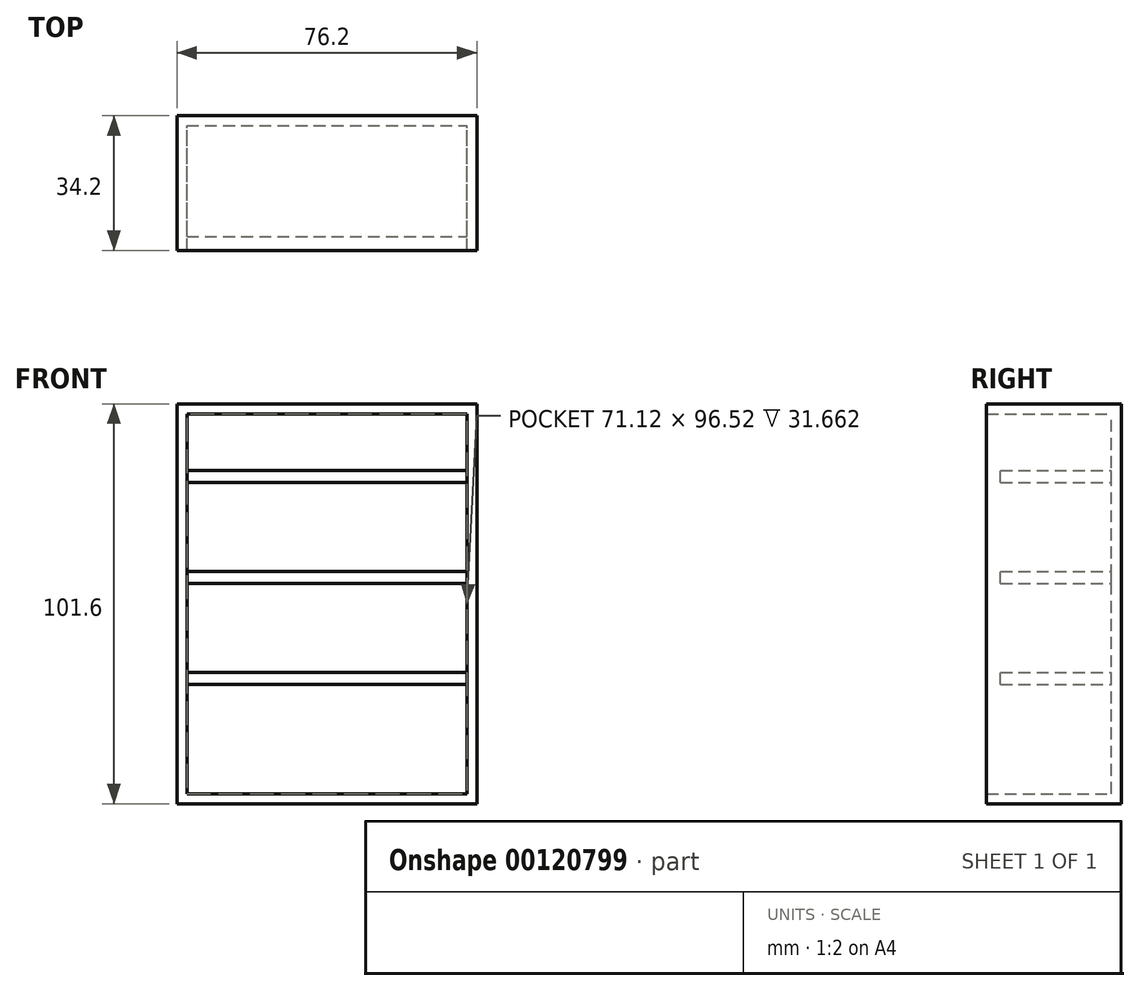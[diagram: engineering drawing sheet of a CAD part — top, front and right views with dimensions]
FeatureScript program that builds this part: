
annotation { "Feature Type Name" : "Feature", "Feature Type Description" : "" }
export const myFeature = defineFeature(function(context is Context, id is Id, definition is map)
    precondition{}
    {
        {
            var Q0;
            Q0=qCreatedBy(makeId("Front.planeOp"),FACE);
            var sketch = newSketch(context, id + "F0", { "sketchPlane" : qUnion([Q0])});
            skLineSegment(sketch, "E0.bottom", {"start": v(0, 0) * mm, "end": v(-76.2, 0) * mm});
            skLineSegment(sketch, "E0.top", {"start": v(0, 101.6) * mm, "end": v(-76.2, 101.6) * mm});
            skLineSegment(sketch, "E0.left", {"start": v(0, 0) * mm, "end": v(0, 101.6) * mm});
            skLineSegment(sketch, "E0.right", {"start": v(-76.2, 0) * mm, "end": v(-76.2, 101.6) * mm});
            skSolve(sketch);
        }
        {
            var Q0;
            Q0=makeQuery(id+"F0.imprint","IMPRINT",FACE,{"disambiguationData":[TD([[makeQuery(id+"F0.imprint","IMPRINT",EDGE,{"derivedFrom":sQuery(id+"F0.wireOp",EDGE,"E0.bottom")}),-1.0]])]});
            extrude(context, id + "F1", {"entities" : qUnion([Q0]), "depth" : 34.2 * mm});
        }
        {
            var Q0;
            Q0=makeQuery(id+"F1.opExtrude","CAP_FACE",FACE,{"disambiguationData":[OSD([sQuery(id+"F0.wireOp",EDGE,"E0.bottom"),sQuery(id+"F0.wireOp",EDGE,"E0.top"),sQuery(id+"F0.wireOp",EDGE,"E0.left"),sQuery(id+"F0.wireOp",EDGE,"E0.right")])],"isStart":false});
            shell(context, id + "F2", {"entities" : qUnion([Q0]), "thickness" : 2.54 * mm});
        }
        {
            var Q0;
            Q0=makeQuery(id+"F2.opShell","OFFSET_FACE",FACE,{"disambiguationData":[OSD([sQuery(id+"F0.wireOp",EDGE,"E0.bottom"),sQuery(id+"F0.wireOp",EDGE,"E0.top"),sQuery(id+"F0.wireOp",EDGE,"E0.left"),sQuery(id+"F0.wireOp",EDGE,"E0.right")])]});
            var sketch = newSketch(context, id + "F3", { "sketchPlane" : qUnion([Q0])});
            skLineSegment(sketch, "E1", {"start": v(-73.66, 84.65) * mm, "end": v(-2.54, 84.65) * mm});
            skLineSegment(sketch, "E2", {"start": v(-2.54, 84.65) * mm, "end": v(-2.54, 81.6) * mm});
            skLineSegment(sketch, "E3", {"start": v(-2.54, 81.6) * mm, "end": v(-73.66, 81.6) * mm});
            skLineSegment(sketch, "E4", {"start": v(-73.66, 81.6) * mm, "end": v(-73.66, 84.65) * mm});
            skLineSegment(sketch, "E5", {"start": v(-73.66, 59) * mm, "end": v(-2.54, 59) * mm});
            skLineSegment(sketch, "E6", {"start": v(-2.54, 59) * mm, "end": v(-2.54, 55.95) * mm});
            skLineSegment(sketch, "E7", {"start": v(-2.54, 55.95) * mm, "end": v(-73.66, 55.95) * mm});
            skLineSegment(sketch, "E8", {"start": v(-73.66, 55.95) * mm, "end": v(-73.66, 59) * mm});
            skLineSegment(sketch, "E9", {"start": v(-73.66, 33.35) * mm, "end": v(-2.54, 33.35) * mm});
            skLineSegment(sketch, "E10", {"start": v(-2.54, 33.35) * mm, "end": v(-2.54, 30.3) * mm});
            skLineSegment(sketch, "E11", {"start": v(-2.54, 30.3) * mm, "end": v(-73.66, 30.3) * mm});
            skLineSegment(sketch, "E12", {"start": v(-73.66, 30.3) * mm, "end": v(-73.66, 33.35) * mm});
            skSolve(sketch);
        }
        {
            var Q0;
            Q0=makeQuery(id+"F3.imprint","IMPRINT",FACE,{"disambiguationData":[TD([[makeQuery(id+"F3.imprint","IMPRINT",EDGE,{"derivedFrom":sQuery(id+"F3.wireOp",EDGE,"E5")}),-1.0]])]});
            var Q1;
            Q1=makeQuery(id+"F3.imprint","IMPRINT",FACE,{"disambiguationData":[TD([[makeQuery(id+"F3.imprint","IMPRINT",EDGE,{"derivedFrom":sQuery(id+"F3.wireOp",EDGE,"E9")}),-1.0]])]});
            var Q2;
            Q2=makeQuery(id+"F3.imprint","IMPRINT",FACE,{"disambiguationData":[TD([[makeQuery(id+"F3.imprint","IMPRINT",EDGE,{"derivedFrom":sQuery(id+"F3.wireOp",EDGE,"E1")}),-1.0]])]});
            extrude(context, id + "F4", {"entities" : qUnion([Q0, Q1, Q2]), "depth" : 28.15 * mm});
        }
    });
